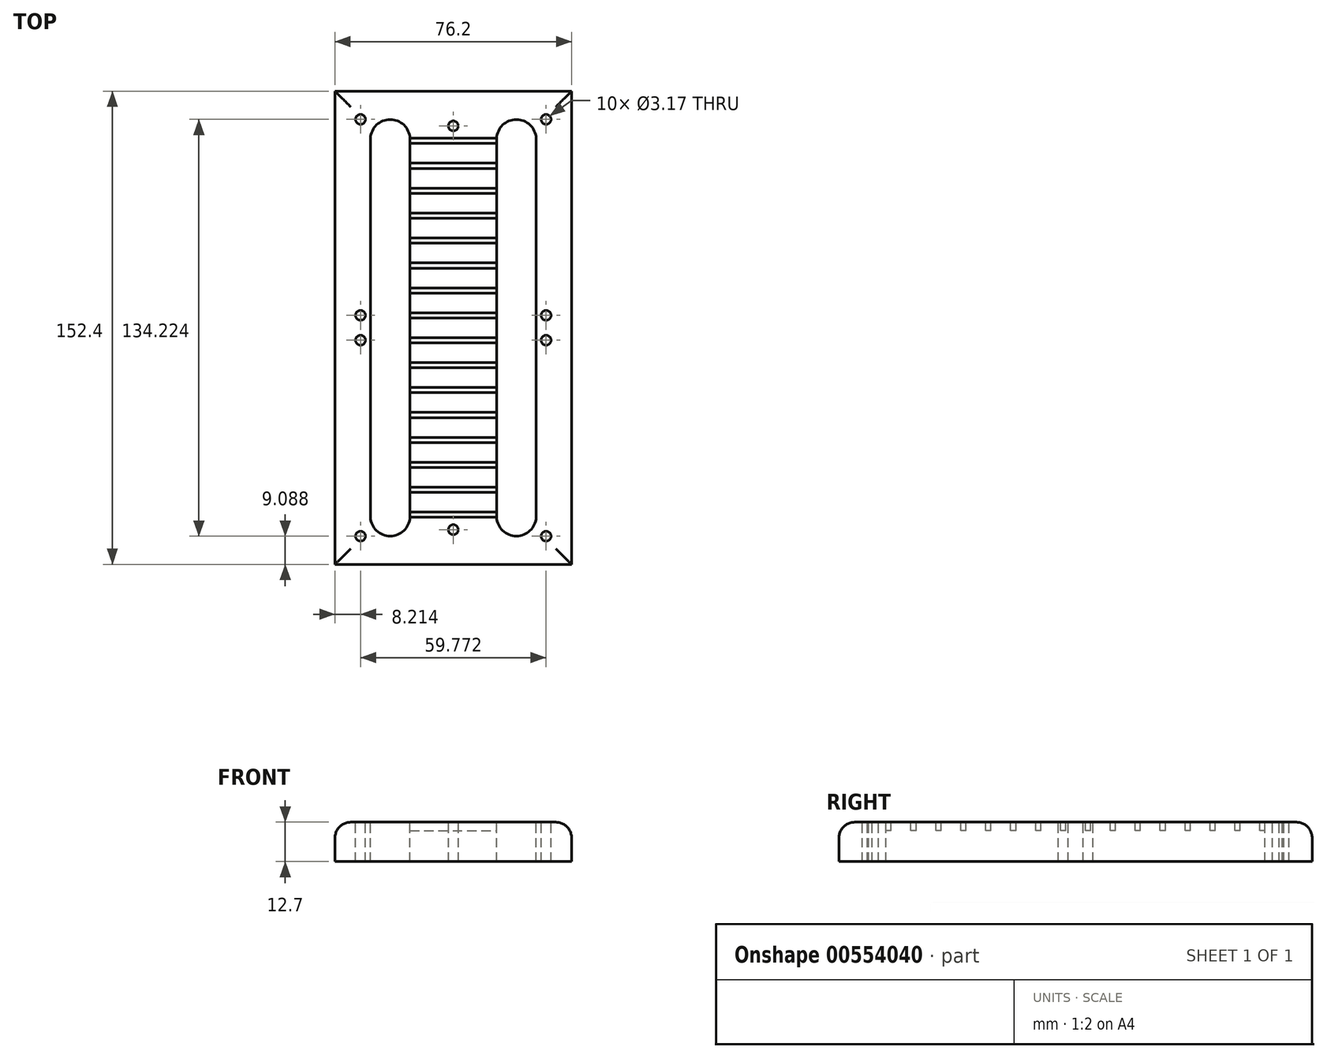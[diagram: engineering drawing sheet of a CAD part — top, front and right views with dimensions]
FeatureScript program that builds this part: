
annotation { "Feature Type Name" : "Feature", "Feature Type Description" : "" }
export const myFeature = defineFeature(function(context is Context, id is Id, definition is map)
    precondition{}
    {
        {
            var Q0;
            Q0=qCreatedBy(makeId("Top.planeOp"),FACE);
            var sketch = newSketch(context, id + "F0", { "sketchPlane" : qUnion([Q0])});
            skLineSegment(sketch, "E0.bottom", {"start": v(38.1, 76.2) * mm, "end": v(-38.1, 76.2) * mm});
            skLineSegment(sketch, "E0.top", {"start": v(38.1, -76.2) * mm, "end": v(-38.1, -76.2) * mm});
            skLineSegment(sketch, "E0.left", {"start": v(38.1, 76.2) * mm, "end": v(38.1, -76.2) * mm});
            skLineSegment(sketch, "E0.right", {"start": v(-38.1, 76.2) * mm, "end": v(-38.1, -76.2) * mm});
            skPoint(sketch, "E0.middle", {"position": v(0, 0) * mm});
            skSolve(sketch);
        }
        {
            var Q0;
            Q0 = qSketchRegion(id + "F0", true);
            extrude(context, id + "F1", {"entities" : qUnion([Q0]), "depth" : 12.7 * mm, "offsetDistance" : 25.4 * mm});
        }
        {
            var Q0;
            Q0=makeQuery(id+"F1.opExtrude","CAP_EDGE",EDGE,{"disambiguationData":[OSD([sQuery(id+"F0.wireOp",EDGE,"E0.right")])],"isStart":false});
            var Q1;
            Q1=makeQuery(id+"F1.opExtrude","CAP_EDGE",EDGE,{"disambiguationData":[OSD([sQuery(id+"F0.wireOp",EDGE,"E0.bottom")])],"isStart":false});
            var Q2;
            Q2=makeQuery(id+"F1.opExtrude","CAP_EDGE",EDGE,{"disambiguationData":[OSD([sQuery(id+"F0.wireOp",EDGE,"E0.left")])],"isStart":false});
            var Q3;
            Q3=makeQuery(id+"F1.opExtrude","CAP_EDGE",EDGE,{"disambiguationData":[OSD([sQuery(id+"F0.wireOp",EDGE,"E0.top")])],"isStart":false});
            fillet(context, id + "F2", {"entities" : qUnion([Q0, Q1, Q2, Q3]), "tangentPropagation" : true, "radius" : 5.08 * mm, "defaultsChanged" : false, "vertexSettings" : [], "allowEdgeOverflow" : false});
        }
        {
            var Q0;
            Q0=makeQuery(id+"F1.opExtrude","CAP_FACE",FACE,{"disambiguationData":[OSD([sQuery(id+"F0.wireOp",EDGE,"E0.bottom"),sQuery(id+"F0.wireOp",EDGE,"E0.top"),sQuery(id+"F0.wireOp",EDGE,"E0.left"),sQuery(id+"F0.wireOp",EDGE,"E0.right")])],"isStart":false});
            var sketch = newSketch(context, id + "F3", { "sketchPlane" : qUnion([Q0])});
            skLineSegment(sketch, "E1", {"start": v(-33.02, 61.03) * mm, "end": v(33.02, 61.03) * mm, "construction": true});
            skLineSegment(sketch, "E2", {"start": v(-33.02, 61.03) * mm, "end": v(-26.67, 61.03) * mm, "construction": true});
            skLineSegment(sketch, "E3", {"start": v(-26.67, 61.03) * mm, "end": v(-13.97, 61.03) * mm, "construction": true});
            skArc(sketch, "E4", {"start": v(-13.97, 61.03) * mm, "mid": v(-20.32, 67.08) * mm, "end": v(-26.67, 61.03) * mm});
            skLineSegment(sketch, "E5", {"start": v(-33.02, 0) * mm, "end": v(33.02, 0) * mm, "construction": true});
            skArc(sketch, "E6.MirrorCS", {"start": v(-13.97, -61.03) * mm, "mid": v(-20.32, -67.08) * mm, "end": v(-26.67, -61.03) * mm});
            skLineSegment(sketch, "E7", {"start": v(0, 61.03) * mm, "end": v(0, 0) * mm, "construction": true});
            skArc(sketch, "E8.MirrorCS", {"start": v(13.97, 61.03) * mm, "mid": v(20.32, 67.08) * mm, "end": v(26.67, 61.03) * mm});
            skArc(sketch, "E9.MirrorCS", {"start": v(13.97, -61.03) * mm, "mid": v(20.32, -67.08) * mm, "end": v(26.67, -61.03) * mm});
            skLineSegment(sketch, "E10", {"start": v(-26.67, 61.03) * mm, "end": v(-26.67, -61.03) * mm});
            skLineSegment(sketch, "E11", {"start": v(-13.97, -61.03) * mm, "end": v(-13.97, 61.03) * mm});
            skLineSegment(sketch, "E12", {"start": v(13.97, 61.03) * mm, "end": v(13.97, -61.03) * mm});
            skLineSegment(sketch, "E13", {"start": v(26.67, -61.03) * mm, "end": v(26.67, 61.03) * mm});
            skSolve(sketch);
        }
        {
            var Q0;
            Q0 = qSketchRegion(id + "F3", true);
            extrude(context, id + "F4", {"entities" : qUnion([Q0]), "operationType" : NewBodyOperationType.REMOVE, "oppositeDirection" : true, "depth" : 25.4 * mm, "offsetDistance" : 25.4 * mm});
        }
        {
            var Q0;
            Q0=makeQuery(id+"F1.opExtrude","CAP_FACE",FACE,{"disambiguationData":[OSD([sQuery(id+"F0.wireOp",EDGE,"E0.bottom"),sQuery(id+"F0.wireOp",EDGE,"E0.top"),sQuery(id+"F0.wireOp",EDGE,"E0.left"),sQuery(id+"F0.wireOp",EDGE,"E0.right")])],"isStart":false});
            var sketch = newSketch(context, id + "F5", { "sketchPlane" : qUnion([Q0])});
            skCircle(sketch, "E14", {"center": v(0, 65.01) * mm, "radius": 1.59 * mm});
            skPoint(sketch, "E14.centerSnap0", {"position": v(0, 71.12) * mm});
            skLineSegment(sketch, "E15", {"start": v(-33.02, 0) * mm, "end": v(33.02, 0) * mm, "construction": true});
            skCircle(sketch, "E16.MirrorC", {"center": v(0, -65.01) * mm, "radius": 1.59 * mm});
            skLineSegment(sketch, "E17", {"start": v(0, 71.12) * mm, "end": v(-33.02, 71.12) * mm, "construction": true});
            skCircle(sketch, "E18", {"center": v(-29.89, 67.11) * mm, "radius": 1.59 * mm});
            skLineSegment(sketch, "E19", {"start": v(0, 71.12) * mm, "end": v(0, -41.32) * mm, "construction": true});
            skCircle(sketch, "E20.MirrorC", {"center": v(29.89, 67.11) * mm, "radius": 1.59 * mm});
            skLineSegment(sketch, "E21.MirrorCS", {"start": v(33.02, 0) * mm, "end": v(-33.02, 0) * mm, "construction": true});
            skCircle(sketch, "E22.MirrorC", {"center": v(29.89, -67.11) * mm, "radius": 1.59 * mm});
            skCircle(sketch, "E23.MirrorC", {"center": v(-29.89, -67.11) * mm, "radius": 1.59 * mm});
            skLineSegment(sketch, "E24", {"start": v(-33.02, 0) * mm, "end": v(-33.02, 71.12) * mm, "construction": true});
            skLineSegment(sketch, "E25", {"start": v(-33.02, 35.56) * mm, "end": v(24.22, 35.56) * mm, "construction": true});
            skCircle(sketch, "E26.MirrorC", {"center": v(-29.89, 4) * mm, "radius": 1.59 * mm});
            skCircle(sketch, "E27.MirrorC", {"center": v(29.89, 4) * mm, "radius": 1.59 * mm});
            skCircle(sketch, "E28.MirrorC", {"center": v(-29.89, -4) * mm, "radius": 1.59 * mm});
            skCircle(sketch, "E29.MirrorC", {"center": v(29.89, -4) * mm, "radius": 1.59 * mm});
            skSolve(sketch);
        }
        {
            var Q0;
            Q0 = qSketchRegion(id + "F5", true);
            extrude(context, id + "F6", {"entities" : qUnion([Q0]), "operationType" : NewBodyOperationType.REMOVE, "oppositeDirection" : true, "depth" : 25.4 * mm, "offsetDistance" : 25.4 * mm});
        }
        {
            var Q0;
            Q0=makeQuery(id+"F1.opExtrude","CAP_FACE",FACE,{"disambiguationData":[OSD([sQuery(id+"F0.wireOp",EDGE,"E0.bottom"),sQuery(id+"F0.wireOp",EDGE,"E0.top"),sQuery(id+"F0.wireOp",EDGE,"E0.left"),sQuery(id+"F0.wireOp",EDGE,"E0.right")])],"isStart":false});
            var sketch = newSketch(context, id + "F7", { "sketchPlane" : qUnion([Q0])});
            skLineSegment(sketch, "E30.bottom", {"start": v(-13.97, 61.03) * mm, "end": v(13.97, 61.03) * mm});
            skLineSegment(sketch, "E30.top", {"start": v(-13.97, 59.35) * mm, "end": v(13.97, 59.35) * mm});
            skLineSegment(sketch, "E30.left", {"start": v(-13.97, 61.03) * mm, "end": v(-13.97, 59.35) * mm});
            skLineSegment(sketch, "E30.right", {"start": v(13.97, 61.03) * mm, "end": v(13.97, 59.35) * mm});
            skLineSegment(sketch, "E31", {"start": v(0, 59.35) * mm, "end": v(0, 53) * mm, "construction": true});
            skLineSegment(sketch, "E32", {"start": v(0, 53) * mm, "end": v(0, 56.18) * mm, "construction": true});
            skLineSegment(sketch, "E33", {"start": v(0, 56.18) * mm, "end": v(13.97, 56.18) * mm, "construction": true});
            skLineSegment(sketch, "E34.MirrorCS", {"start": v(-13.97, 53) * mm, "end": v(13.97, 53) * mm});
            skLineSegment(sketch, "E35.MirrorCS", {"start": v(-13.97, 51.32) * mm, "end": v(13.97, 51.32) * mm});
            skLineSegment(sketch, "E36", {"start": v(0, 51.32) * mm, "end": v(0, 44.97) * mm, "construction": true});
            skLineSegment(sketch, "E37", {"start": v(0, 44.97) * mm, "end": v(0, 48.15) * mm, "construction": true});
            skLineSegment(sketch, "E38", {"start": v(0, 48.15) * mm, "end": v(11.58, 48.15) * mm, "construction": true});
            skLineSegment(sketch, "E39.MirrorCS", {"start": v(-13.97, 44.97) * mm, "end": v(13.97, 44.97) * mm});
            skLineSegment(sketch, "E40.MirrorCS", {"start": v(-13.97, 43.3) * mm, "end": v(13.97, 43.3) * mm});
            skLineSegment(sketch, "E41.MirrorCS", {"start": v(-13.97, 36.95) * mm, "end": v(13.97, 36.95) * mm});
            skLineSegment(sketch, "E42.MirrorCS", {"start": v(-13.97, 35.27) * mm, "end": v(13.97, 35.27) * mm});
            skLineSegment(sketch, "E43", {"start": v(0, 35.27) * mm, "end": v(0, 28.92) * mm, "construction": true});
            skLineSegment(sketch, "E44", {"start": v(0, 28.92) * mm, "end": v(0, 32.1) * mm, "construction": true});
            skLineSegment(sketch, "E45", {"start": v(0, 32.1) * mm, "end": v(6.97, 32.1) * mm, "construction": true});
            skLineSegment(sketch, "E46.MirrorCS", {"start": v(-13.97, 28.92) * mm, "end": v(13.97, 28.92) * mm});
            skLineSegment(sketch, "E47.MirrorCS", {"start": v(-13.97, 27.24) * mm, "end": v(13.97, 27.24) * mm});
            skLineSegment(sketch, "E48.MirrorCS", {"start": v(-13.97, 19.21) * mm, "end": v(13.97, 19.21) * mm});
            skLineSegment(sketch, "E49.MirrorCS", {"start": v(-13.97, 20.9) * mm, "end": v(13.97, 20.9) * mm});
            skLineSegment(sketch, "E50.MirrorCS", {"start": v(-13.97, 12.86) * mm, "end": v(13.97, 12.86) * mm});
            skLineSegment(sketch, "E51.MirrorCS", {"start": v(-13.97, 11.19) * mm, "end": v(13.97, 11.19) * mm});
            skLineSegment(sketch, "E52.MirrorCS", {"start": v(-13.97, 4.84) * mm, "end": v(13.97, 4.84) * mm});
            skLineSegment(sketch, "E53.MirrorCS", {"start": v(-13.97, 3.16) * mm, "end": v(13.97, 3.16) * mm});
            skLineSegment(sketch, "E54", {"start": v(0, 3.16) * mm, "end": v(0, -3.2) * mm, "construction": true});
            skLineSegment(sketch, "E55", {"start": v(0, -3.2) * mm, "end": v(0, 0) * mm, "construction": true});
            skLineSegment(sketch, "E56", {"start": v(4.34, 0) * mm, "end": v(0, 0) * mm, "construction": true});
            skLineSegment(sketch, "E57.MirrorCS", {"start": v(-13.97, -3.16) * mm, "end": v(13.97, -3.16) * mm});
            skLineSegment(sketch, "E58.MirrorCS", {"start": v(-13.97, -4.84) * mm, "end": v(13.97, -4.84) * mm});
            skLineSegment(sketch, "E59.MirrorCS", {"start": v(-13.97, -11.19) * mm, "end": v(13.97, -11.19) * mm});
            skLineSegment(sketch, "E60.MirrorCS", {"start": v(-13.97, -12.86) * mm, "end": v(13.97, -12.86) * mm});
            skLineSegment(sketch, "E61.MirrorCS", {"start": v(-13.97, -19.21) * mm, "end": v(13.97, -19.21) * mm});
            skLineSegment(sketch, "E62.MirrorCS", {"start": v(-13.97, -20.9) * mm, "end": v(13.97, -20.9) * mm});
            skLineSegment(sketch, "E63.MirrorCS", {"start": v(-13.97, -27.24) * mm, "end": v(13.97, -27.24) * mm});
            skLineSegment(sketch, "E64.MirrorCS", {"start": v(-13.97, -28.92) * mm, "end": v(13.97, -28.92) * mm});
            skLineSegment(sketch, "E65.MirrorCS", {"start": v(-13.97, -35.27) * mm, "end": v(13.97, -35.27) * mm});
            skLineSegment(sketch, "E66.MirrorCS", {"start": v(-13.97, -36.95) * mm, "end": v(13.97, -36.95) * mm});
            skLineSegment(sketch, "E67.MirrorCS", {"start": v(-13.97, -43.3) * mm, "end": v(13.97, -43.3) * mm});
            skLineSegment(sketch, "E68.MirrorCS", {"start": v(-13.97, -44.97) * mm, "end": v(13.97, -44.97) * mm});
            skLineSegment(sketch, "E69.MirrorCS", {"start": v(-13.97, -51.32) * mm, "end": v(13.97, -51.32) * mm});
            skLineSegment(sketch, "E70.MirrorCS", {"start": v(-13.97, -53) * mm, "end": v(13.97, -53) * mm});
            skLineSegment(sketch, "E71.MirrorCS", {"start": v(-13.97, -59.35) * mm, "end": v(13.97, -59.35) * mm});
            skLineSegment(sketch, "E72.MirrorCS", {"start": v(-13.97, -61.03) * mm, "end": v(13.97, -61.03) * mm});
            skSolve(sketch);
        }
        {
            var Q0;
            Q0 = qSketchRegion(id + "F7", true);
            var Q1;
            {var subQ0=sQuery(id+"F7.wireOp",EDGE,"E34.MirrorCS");Q1=makeQuery(id+"F7.imprint","IMPRINT",FACE,{"disambiguationData":[TD([[makeQuery(id+"F7.imprint","IMPRINT",EDGE,{"derivedFrom":subQ0}),-1.0]])]});}
            var Q2;
            {var subQ0=sQuery(id+"F7.wireOp",EDGE,"E39.MirrorCS");Q2=makeQuery(id+"F7.imprint","IMPRINT",FACE,{"disambiguationData":[TD([[makeQuery(id+"F7.imprint","IMPRINT",EDGE,{"derivedFrom":subQ0}),-1.0]])]});}
            var Q3;
            {var subQ0=sQuery(id+"F7.wireOp",EDGE,"E41.MirrorCS");Q3=makeQuery(id+"F7.imprint","IMPRINT",FACE,{"disambiguationData":[TD([[makeQuery(id+"F7.imprint","IMPRINT",EDGE,{"derivedFrom":subQ0}),-1.0]])]});}
            var Q4;
            {var subQ0=sQuery(id+"F7.wireOp",EDGE,"E46.MirrorCS");Q4=makeQuery(id+"F7.imprint","IMPRINT",FACE,{"disambiguationData":[TD([[makeQuery(id+"F7.imprint","IMPRINT",EDGE,{"derivedFrom":subQ0}),-1.0]])]});}
            var Q5;
            {var subQ0=sQuery(id+"F7.wireOp",EDGE,"E48.MirrorCS");Q5=makeQuery(id+"F7.imprint","IMPRINT",FACE,{"disambiguationData":[TD([[makeQuery(id+"F7.imprint","IMPRINT",EDGE,{"derivedFrom":subQ0}),1.0]])]});}
            var Q6;
            {var subQ0=sQuery(id+"F7.wireOp",EDGE,"E50.MirrorCS");Q6=makeQuery(id+"F7.imprint","IMPRINT",FACE,{"disambiguationData":[TD([[makeQuery(id+"F7.imprint","IMPRINT",EDGE,{"derivedFrom":subQ0}),-1.0]])]});}
            var Q7;
            {var subQ0=sQuery(id+"F7.wireOp",EDGE,"E52.MirrorCS");Q7=makeQuery(id+"F7.imprint","IMPRINT",FACE,{"disambiguationData":[TD([[makeQuery(id+"F7.imprint","IMPRINT",EDGE,{"derivedFrom":subQ0}),-1.0]])]});}
            var Q8;
            {var subQ0=sQuery(id+"F7.wireOp",EDGE,"E57.MirrorCS");Q8=makeQuery(id+"F7.imprint","IMPRINT",FACE,{"disambiguationData":[TD([[makeQuery(id+"F7.imprint","IMPRINT",EDGE,{"derivedFrom":subQ0}),-1.0]])]});}
            var Q9;
            {var subQ0=sQuery(id+"F7.wireOp",EDGE,"E59.MirrorCS");Q9=makeQuery(id+"F7.imprint","IMPRINT",FACE,{"disambiguationData":[TD([[makeQuery(id+"F7.imprint","IMPRINT",EDGE,{"derivedFrom":subQ0}),-1.0]])]});}
            var Q10;
            {var subQ0=sQuery(id+"F7.wireOp",EDGE,"E61.MirrorCS");Q10=makeQuery(id+"F7.imprint","IMPRINT",FACE,{"disambiguationData":[TD([[makeQuery(id+"F7.imprint","IMPRINT",EDGE,{"derivedFrom":subQ0}),-1.0]])]});}
            var Q11;
            {var subQ0=sQuery(id+"F7.wireOp",EDGE,"E63.MirrorCS");Q11=makeQuery(id+"F7.imprint","IMPRINT",FACE,{"disambiguationData":[TD([[makeQuery(id+"F7.imprint","IMPRINT",EDGE,{"derivedFrom":subQ0}),-1.0]])]});}
            var Q12;
            {var subQ0=sQuery(id+"F7.wireOp",EDGE,"E65.MirrorCS");Q12=makeQuery(id+"F7.imprint","IMPRINT",FACE,{"disambiguationData":[TD([[makeQuery(id+"F7.imprint","IMPRINT",EDGE,{"derivedFrom":subQ0}),-1.0]])]});}
            var Q13;
            {var subQ0=sQuery(id+"F7.wireOp",EDGE,"E67.MirrorCS");Q13=makeQuery(id+"F7.imprint","IMPRINT",FACE,{"disambiguationData":[TD([[makeQuery(id+"F7.imprint","IMPRINT",EDGE,{"derivedFrom":subQ0}),-1.0]])]});}
            var Q14;
            {var subQ0=sQuery(id+"F7.wireOp",EDGE,"E69.MirrorCS");Q14=makeQuery(id+"F7.imprint","IMPRINT",FACE,{"disambiguationData":[TD([[makeQuery(id+"F7.imprint","IMPRINT",EDGE,{"derivedFrom":subQ0}),-1.0]])]});}
            var Q15;
            {var subQ0=sQuery(id+"F7.wireOp",EDGE,"E71.MirrorCS");Q15=makeQuery(id+"F7.imprint","IMPRINT",FACE,{"disambiguationData":[TD([[makeQuery(id+"F7.imprint","IMPRINT",EDGE,{"derivedFrom":subQ0}),-1.0]])]});}
            extrude(context, id + "F8", {"entities" : qUnion([Q0, Q1, Q2, Q3, Q4, Q5, Q6, Q7, Q8, Q9, Q10, Q11, Q12, Q13, Q14, Q15]), "operationType" : NewBodyOperationType.REMOVE, "oppositeDirection" : true, "depth" : 2.8 * mm, "offsetDistance" : 25.4 * mm});
        }
    });
